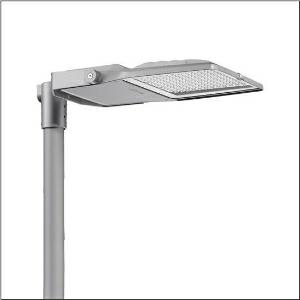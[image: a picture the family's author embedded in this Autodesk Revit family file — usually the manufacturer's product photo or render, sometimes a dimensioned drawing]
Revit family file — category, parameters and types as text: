
# Revit family: floodlight_fl_21_midi___pl43_5xa7785e2a3a_e2fe
name_source: partatom
category: Lighting Fixtures
units: mm (PartAtom-declared; Revit-internal decimal feet)

## family parameters
Cut with Voids When Loaded = No
Host = Face
Light Source = No
Part Type = Normal
Room Calculation Point = No
Round Connector Dimension = Use Diameter
Shared = No

## types (1)
- --- (1 x LED, 27640 lm, 212.4 W, 3000K)
    Apparent Load = 212 VA
    CIE Flux Codes = 27 78 99 100 100
    Color Rendering = 70
    Color Temperature = 3000K
    Default Elevation = 1800 mm
    Description = Floodlight FL 21 midi, floodlight, primary light control with lens, of PMMA, primary optical cover: protective disc, of toughened safety glass, transparent, light distribution: PL43, light emission: direct distribution, installation type: surface-mounted, LED, High Power LED, rated luminous flux: 27.640lm, luminous efficacy: 130lm/W, light colour: 730, colour temperature: 3000K, control gear: Smart Interface (Zhaga), control: flexible luminous flux parameterisation, time-dependent luminous flux control, constant luminous flux control, overheat protection, pre-setting: logarithmic dimming characteristic, with terminal, 6-pole, mains connection: 220..240V, AC, 50/60Hz, start of lifetime: 212W, end of service life: 231W, reduction: 95W, luminaire housing, of diecast aluminium, powder-coated, Siteco® metallic grey (DB 702S), corrosivity category C5 mid according to DIN EN ISO 12944, suitable for swimming pools, chlorine-resistant, sealing non-destructively replaceable, please order mast flange separately, mast bracket, of steel, galvanised, powder-coated, Siteco® metallic grey (DB 702S), Smart Interface above, protection rating (complete): IP66, insulation class (complete): insulation class II (safety insulation), certification: CE, ENEC, VDE, protection symbol: D, impact resistance: IK08, permissible operating ambient temperature: -20..+40°C, permissible operating ambient temperature for outdoor applications: -40..+50°C, standard: DIN EN 12944, LABS conformity tested according to VDMA 24364:2018-05, packaging unit: 1 piece

Light Distribution: PL43
    Height = 76 mm
    Lamp = 1 x LED
    Lamp Light Flux = 27640 lm
    Lamp Power = 212.4 W
    Lamp count = 1
    Length = 657 mm
    Luminous efficacy = 130 lm/W
    Manufacturer = Siteco
    ModVariant = No
    Model = 5XA7785E2A3A
    Number of Poles = 1
    OnlyDefault = Yes
    Power Factor = 1
    Product Name = Floodlight FL 21 midi | PL43
    Product group = floodlight | pylon annexe
    ProductGroupID = 6201
    Protection Class = Protection class II
    Protection Degree = IP 66
    RLX_Detail_Level = 1
    RLX_Emergency_Light_Flux = 0 lm
    RLX_Emergency_Type = 0
    RLX_Emergency_Type_DB = No
    RlxData = <blob elided: 153609 chars, md5=a1b153b8>
    Socket = socket
    Standby Power = 0 W
    System Light Flux = 27640 lm
    System Power = 212 W
    Type Comments = factory setting: luminous flux: 100 % | dim-lin: 254 | 710 mA
    Type Image = l_1007123.jpg
    URL = http://relux.com
    VarID = @adj_198795
    Voltage = 0 V
    Weight = 0.00 kg
    Width = 442 mm

## geometry (parser evidence)
native form markers: Blend x4, Sweep x15
no freeform markers — native parametric forms only
